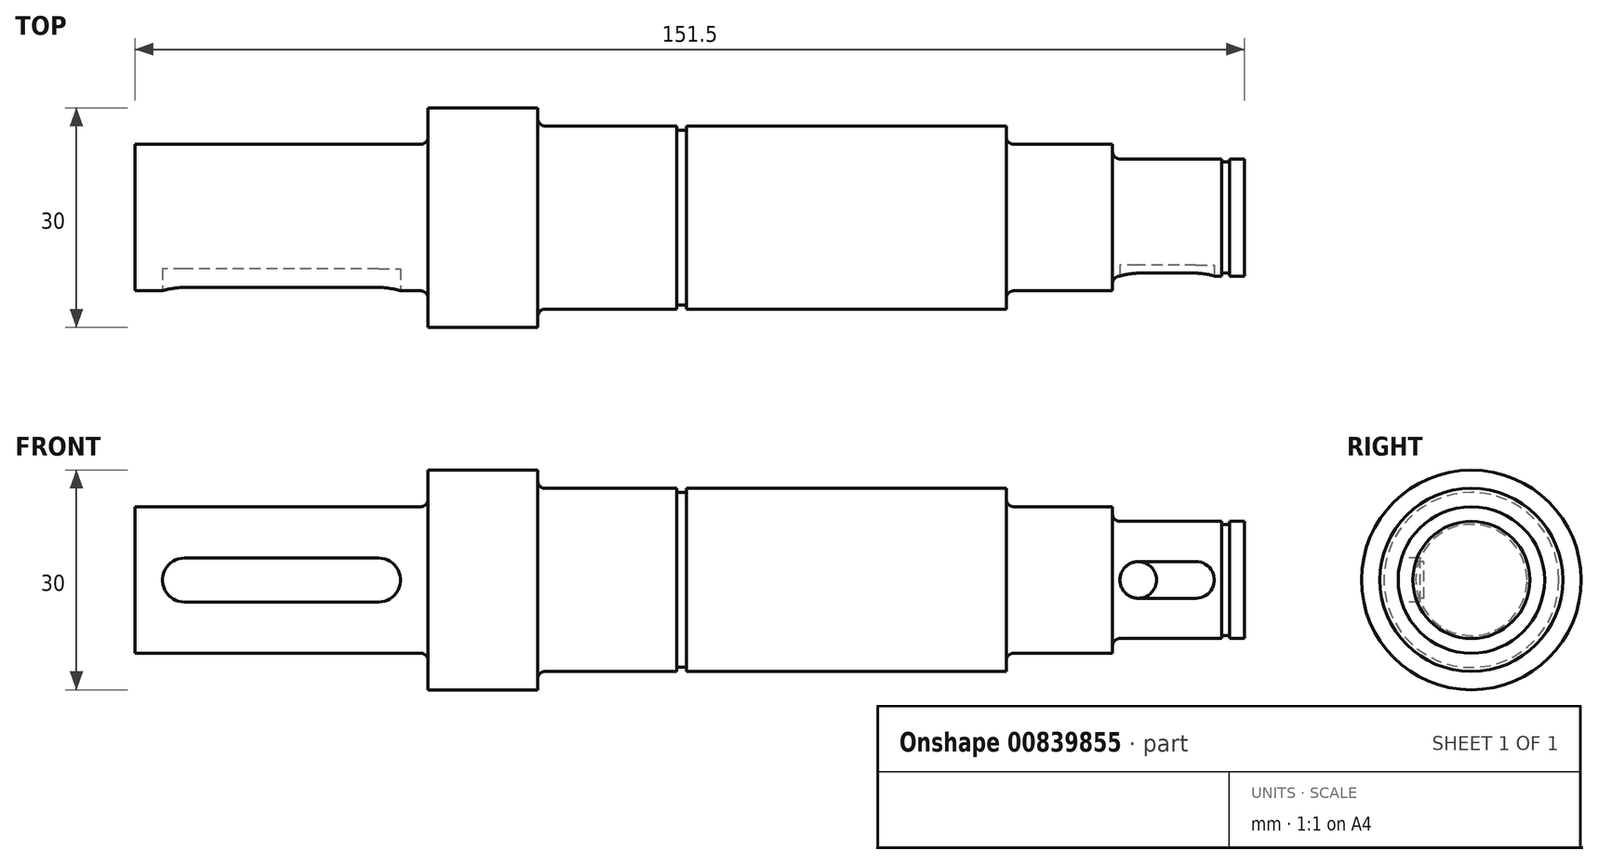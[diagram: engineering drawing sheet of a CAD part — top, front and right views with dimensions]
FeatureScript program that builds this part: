
annotation { "Feature Type Name" : "Feature", "Feature Type Description" : "" }
export const myFeature = defineFeature(function(context is Context, id is Id, definition is map)
    precondition{}
    {
        {
            var Q0;
            Q0=qCreatedBy(makeId("Front.planeOp"),FACE);
            var sketch = newSketch(context, id + "F0", { "sketchPlane" : qUnion([Q0])});
            skLineSegment(sketch, "E0", {"start": v(-106.5, 0) * mm, "end": v(124.46, 0) * mm, "construction": true});
            skLineSegment(sketch, "E1", {"start": v(-75.75, 0) * mm, "end": v(-75.75, 10) * mm});
            skLineSegment(sketch, "E2", {"start": v(-75.75, 10) * mm, "end": v(-35.75, 10) * mm});
            skLineSegment(sketch, "E3", {"start": v(-35.75, 10) * mm, "end": v(-35.75, 15) * mm});
            skLineSegment(sketch, "E4", {"start": v(-35.75, 15) * mm, "end": v(-20.75, 15) * mm});
            skLineSegment(sketch, "E5", {"start": v(-20.75, 15) * mm, "end": v(-20.75, 12.5) * mm});
            skLineSegment(sketch, "E6", {"start": v(-20.75, 12.5) * mm, "end": v(-1.75, 12.5) * mm});
            skLineSegment(sketch, "E7", {"start": v(43.25, 12.5) * mm, "end": v(43.25, 10) * mm});
            skLineSegment(sketch, "E8", {"start": v(43.25, 10) * mm, "end": v(57.75, 10) * mm});
            skLineSegment(sketch, "E9", {"start": v(57.75, 10) * mm, "end": v(57.75, 8) * mm});
            skLineSegment(sketch, "E10", {"start": v(57.75, 8) * mm, "end": v(72.65, 8) * mm});
            skLineSegment(sketch, "E11", {"start": v(75.75, 8) * mm, "end": v(75.75, 0) * mm});
            skLineSegment(sketch, "E12", {"start": v(-1.75, 12.5) * mm, "end": v(-1.75, 11.95) * mm});
            skLineSegment(sketch, "E13", {"start": v(-1.75, 11.95) * mm, "end": v(-0.45, 11.95) * mm});
            skLineSegment(sketch, "E14", {"start": v(-0.45, 11.95) * mm, "end": v(-0.45, 12.5) * mm});
            skLineSegment(sketch, "E15.trimOffspring", {"start": v(-0.45, 12.5) * mm, "end": v(43.25, 12.5) * mm});
            skLineSegment(sketch, "E16", {"start": v(-75.75, 0) * mm, "end": v(75.75, 0) * mm});
            skLineSegment(sketch, "E17", {"start": v(72.65, 8) * mm, "end": v(72.65, 7.6) * mm});
            skLineSegment(sketch, "E18", {"start": v(72.65, 7.6) * mm, "end": v(73.75, 7.6) * mm});
            skLineSegment(sketch, "E19", {"start": v(73.75, 7.6) * mm, "end": v(73.75, 8) * mm});
            skLineSegment(sketch, "E20.trimOffspring", {"start": v(73.75, 8) * mm, "end": v(75.75, 8) * mm});
            skSolve(sketch);
        }
        {
            var Q0;
            Q0=makeQuery(id+"F0.imprint","IMPRINT",FACE,{"disambiguationData":[TD([[makeQuery(id+"F0.imprint","IMPRINT",EDGE,{"derivedFrom":sQuery(id+"F0.wireOp",EDGE,"E1")}),-1.0]])]});
            var Q1;
            Q1=sQuery(id+"F0.wireOp",EDGE,"E0");
            revolve(context, id + "F1", {"surfaceOperationType" : NewSurfaceOperationType.NEW, "entities" : qUnion([Q0]), "axis" : qUnion([Q1]), "revolveType" : RevolveType.FULL});
        }
        {
            var Q0;
            Q0=qCreatedBy(makeId("Front.planeOp"),FACE);
            cPlane(context, id + "F2", {"entities" : qUnion([Q0]), "cplaneType" : CPlaneType.OFFSET, "offset" : 10 * mm, "width" : 150 * mm, "height" : 150 * mm});
        }
        {
            var Q0;
            Q0=qCreatedBy(id+"F2.planeOp",FACE);
            var sketch = newSketch(context, id + "F3", { "sketchPlane" : qUnion([Q0])});
            skLineSegment(sketch, "E21.bottom", {"start": v(-42.5, -3) * mm, "end": v(-69, -3) * mm});
            skLineSegment(sketch, "E21.top", {"start": v(-42.5, 3) * mm, "end": v(-69, 3) * mm});
            skLineSegment(sketch, "E21.left", {"start": v(-39.5, 0) * mm, "end": v(-39.5, 0) * mm});
            skLineSegment(sketch, "E21.right", {"start": v(-72, 0) * mm, "end": v(-72, 0) * mm});
            skPoint(sketch, "E21.middle", {"position": v(-55.75, 0) * mm});
            skPoint(sketch, "E22.visualSharp", {"position": v(-39.5, 3) * mm});
            skArc(sketch, "E22.filletArc", {"start": v(-39.5, 0) * mm, "mid": v(-40.38, 2.12) * mm, "end": v(-42.5, 3) * mm});
            skPoint(sketch, "E23.visualSharp", {"position": v(-39.5, -3) * mm});
            skArc(sketch, "E23.filletArc", {"start": v(-42.5, -3) * mm, "mid": v(-40.38, -2.12) * mm, "end": v(-39.5, 0) * mm});
            skPoint(sketch, "E24.visualSharp", {"position": v(-72, -3) * mm});
            skArc(sketch, "E24.filletArc", {"start": v(-72, 0) * mm, "mid": v(-71.12, -2.12) * mm, "end": v(-69, -3) * mm});
            skPoint(sketch, "E25.visualSharp", {"position": v(-72, 3) * mm});
            skArc(sketch, "E25.filletArc", {"start": v(-69, 3) * mm, "mid": v(-71.12, 2.12) * mm, "end": v(-72, 0) * mm});
            skLineSegment(sketch, "E26.bottom", {"start": v(69.15, -2.5) * mm, "end": v(61.25, -2.5) * mm});
            skLineSegment(sketch, "E26.top", {"start": v(69.15, 2.5) * mm, "end": v(61.25, 2.5) * mm});
            skLineSegment(sketch, "E26.left", {"start": v(71.65, 0) * mm, "end": v(71.65, 0) * mm});
            skLineSegment(sketch, "E26.right", {"start": v(58.75, 0) * mm, "end": v(58.75, 0) * mm});
            skPoint(sketch, "E26.middle", {"position": v(65.2, 0) * mm});
            skPoint(sketch, "E27.visualSharp", {"position": v(71.65, 2.5) * mm});
            skArc(sketch, "E27.filletArc", {"start": v(71.65, 0) * mm, "mid": v(70.92, 1.77) * mm, "end": v(69.15, 2.5) * mm});
            skPoint(sketch, "E28.visualSharp", {"position": v(71.65, -2.5) * mm});
            skArc(sketch, "E28.filletArc", {"start": v(69.15, -2.5) * mm, "mid": v(70.92, -1.77) * mm, "end": v(71.65, 0) * mm});
            skPoint(sketch, "E29.visualSharp", {"position": v(58.75, -2.5) * mm});
            skArc(sketch, "E29.filletArc", {"start": v(58.75, 0) * mm, "mid": v(59.48, -1.77) * mm, "end": v(61.25, -2.5) * mm});
            skPoint(sketch, "E30.visualSharp", {"position": v(58.75, 2.5) * mm});
            skArc(sketch, "E30.filletArc", {"start": v(61.25, 2.5) * mm, "mid": v(59.48, 1.77) * mm, "end": v(58.75, 0) * mm});
            skSolve(sketch);
        }
        {
            var Q0;
            Q0=makeQuery(id+"F3.imprint","IMPRINT",FACE,{"disambiguationData":[TD([[makeQuery(id+"F3.imprint","IMPRINT",EDGE,{"derivedFrom":sQuery(id+"F3.wireOp",EDGE,"E26.bottom")}),-1.0]])]});
            extrude(context, id + "F4", {"entities" : qUnion([Q0]), "operationType" : NewBodyOperationType.REMOVE, "oppositeDirection" : true, "depth" : 3.5 * mm, "offsetDistance" : 25 * mm});
        }
        {
            var Q0;
            Q0=makeQuery(id+"F3.imprint","IMPRINT",FACE,{"disambiguationData":[TD([[makeQuery(id+"F3.imprint","IMPRINT",EDGE,{"derivedFrom":sQuery(id+"F3.wireOp",EDGE,"E21.bottom")}),-1.0]])]});
            extrude(context, id + "F5", {"entities" : qUnion([Q0]), "operationType" : NewBodyOperationType.REMOVE, "oppositeDirection" : true, "depth" : 3 * mm, "offsetDistance" : 25 * mm});
        }
        {
            var Q0;
            Q0=makeQuery(id+"F1.opRevolve","SWEPT_EDGE",EDGE,{"disambiguationData":[OSD([sQuery(id+"F0.wireOp",EDGE,"E2"),sQuery(id+"F0.wireOp",EDGE,"E3")])]});
            var Q1;
            Q1=makeQuery(id+"F1.opRevolve","SWEPT_EDGE",EDGE,{"disambiguationData":[OSD([sQuery(id+"F0.wireOp",EDGE,"E5"),sQuery(id+"F0.wireOp",EDGE,"E6")])]});
            var Q2;
            Q2=makeQuery(id+"F1.opRevolve","SWEPT_EDGE",EDGE,{"disambiguationData":[OSD([sQuery(id+"F0.wireOp",EDGE,"E7"),sQuery(id+"F0.wireOp",EDGE,"E8")])]});
            var Q3;
            Q3=makeQuery(id+"F1.opRevolve","SWEPT_EDGE",EDGE,{"disambiguationData":[OSD([sQuery(id+"F0.wireOp",EDGE,"E9"),sQuery(id+"F0.wireOp",EDGE,"E10")])]});
            fillet(context, id + "F6", {"entities" : qUnion([Q0, Q1, Q2, Q3]), "radius" : 1 * mm, "tangentPropagation" : true, "allowEdgeOverflow" : false});
        }
    });
